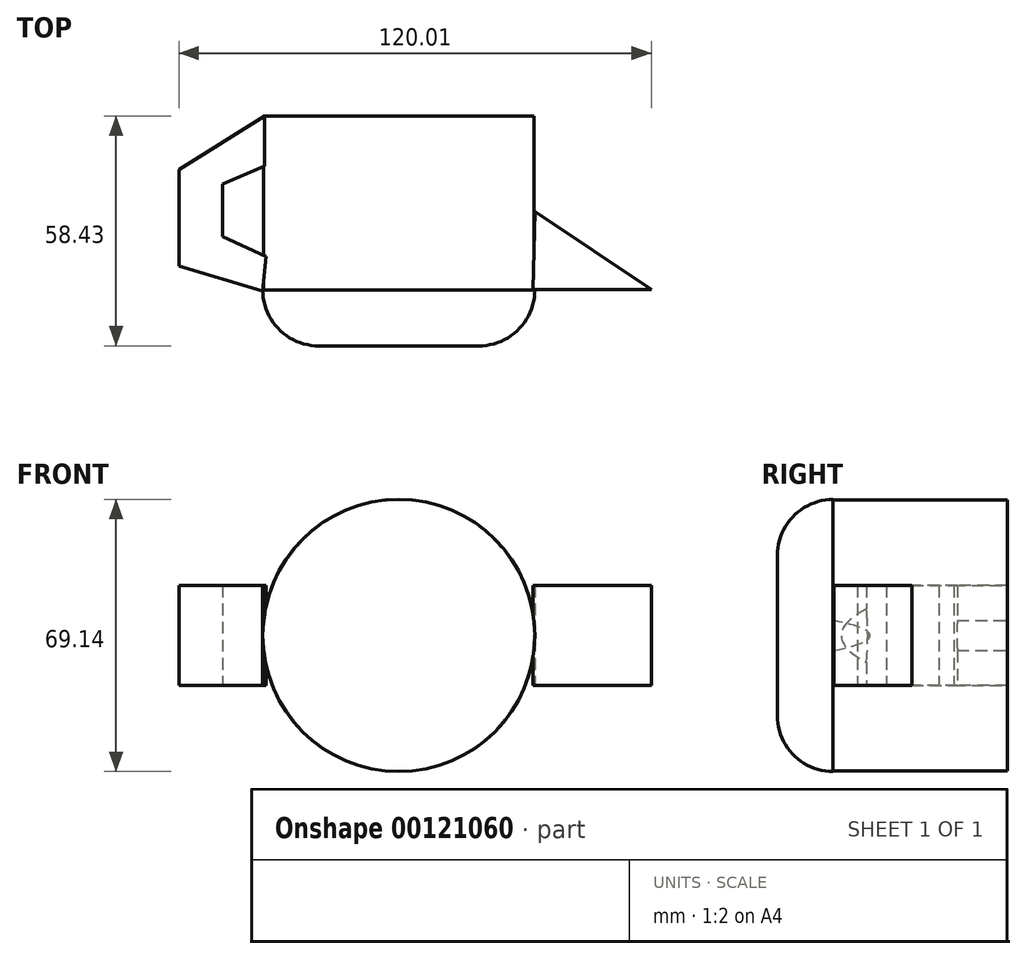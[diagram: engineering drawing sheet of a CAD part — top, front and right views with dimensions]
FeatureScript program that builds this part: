
annotation { "Feature Type Name" : "Feature", "Feature Type Description" : "" }
export const myFeature = defineFeature(function(context is Context, id is Id, definition is map)
    precondition{}
    {
        {
            var Q0;
            Q0=qCreatedBy(makeId("Front.planeOp"),FACE);
            var sketch = newSketch(context, id + "F0", { "sketchPlane" : qUnion([Q0])});
            skCircle(sketch, "E0", {"center": v(0, 0) * mm, "radius": 34.37 * mm});
            skSolve(sketch);
        }
        {
            var Q0;
            Q0 = qSketchRegion(id + "F0", true);
            extrude(context, id + "F1", {"entities" : qUnion([Q0]), "depth" : 44.3 * mm});
        }
        {
            var Q0;
            Q0=makeQuery(id+"F1.opExtrude","CAP_FACE",FACE,{"disambiguationData":[OSD([sQuery(id+"F0.wireOp",EDGE,"E0")])],"isStart":false});
            var sketch = newSketch(context, id + "F2", { "sketchPlane" : qUnion([Q0])});
            skCircle(sketch, "E1", {"center": v(0, 0) * mm, "radius": 34.57 * mm});
            skSolve(sketch);
        }
        {
            var Q0;
            Q0 = qSketchRegion(id + "F2", true);
            extrude(context, id + "F3", {"entities" : qUnion([Q0]), "operationType" : NewBodyOperationType.ADD, "depth" : 14.14 * mm});
        }
        {
            var Q0;
            Q0=makeQuery(id+"F3.opExtrude","CAP_EDGE",EDGE,{"disambiguationData":[OSD([sQuery(id+"F2.wireOp",EDGE,"E1")])],"isStart":false});
            fillet(context, id + "F4", {"entities" : qUnion([Q0]), "radius" : 14.22 * mm, "tangentPropagation" : true, "allowEdgeOverflow" : false});
        }
        {
            var Q0;
            Q0=qCreatedBy(makeId("Top.planeOp"),FACE);
            var sketch = newSketch(context, id + "F5", { "sketchPlane" : qUnion([Q0])});
            skLineSegment(sketch, "E2", {"start": v(34.16, -44.08) * mm, "end": v(64.16, -44.08) * mm});
            skLineSegment(sketch, "E3", {"start": v(64.16, -44.08) * mm, "end": v(34.62, -24.23) * mm});
            skLineSegment(sketch, "E4", {"start": v(34.62, -24.23) * mm, "end": v(34.16, -44.08) * mm});
            skSolve(sketch);
        }
        {
            var Q0;
            Q0=makeQuery(id+"F5.imprint","IMPRINT",FACE,{"disambiguationData":[TD([[makeQuery(id+"F5.imprint","IMPRINT",EDGE,{"derivedFrom":sQuery(id+"F5.wireOp",EDGE,"E2")}),1.0]])]});
            extrude(context, id + "F6", {"entities" : qUnion([Q0]), "operationType" : NewBodyOperationType.ADD, "endBound" : BoundingType.SYMMETRIC, "depth" : 25.4 * mm});
        }
        {
            var Q0;
            Q0=qCreatedBy(makeId("Top.planeOp"),FACE);
            var sketch = newSketch(context, id + "F7", { "sketchPlane" : qUnion([Q0])});
            skLineSegment(sketch, "E5", {"start": v(-34.62, -44.54) * mm, "end": v(-55.85, -38.08) * mm});
            skLineSegment(sketch, "E6", {"start": v(-55.85, -38.08) * mm, "end": v(-55.85, -13.62) * mm});
            skLineSegment(sketch, "E7", {"start": v(-55.85, -13.62) * mm, "end": v(-34.16, 0) * mm});
            skLineSegment(sketch, "E8", {"start": v(-34.16, 0) * mm, "end": v(-34.16, -12.7) * mm});
            skLineSegment(sketch, "E9", {"start": v(-34.16, -12.7) * mm, "end": v(-44.77, -17.3) * mm});
            skLineSegment(sketch, "E10", {"start": v(-44.77, -17.3) * mm, "end": v(-44.77, -30.7) * mm});
            skLineSegment(sketch, "E11", {"start": v(-44.77, -30.7) * mm, "end": v(-33.7, -35.77) * mm});
            skLineSegment(sketch, "E12", {"start": v(-33.7, -35.77) * mm, "end": v(-34.62, -44.54) * mm});
            skSolve(sketch);
        }
        {
            var Q0;
            Q0=makeQuery(id+"F7.imprint","IMPRINT",FACE,{"disambiguationData":[TD([[makeQuery(id+"F7.imprint","IMPRINT",EDGE,{"derivedFrom":sQuery(id+"F7.wireOp",EDGE,"E5")}),-1.0]])]});
            extrude(context, id + "F8", {"entities" : qUnion([Q0]), "operationType" : NewBodyOperationType.ADD, "endBound" : BoundingType.SYMMETRIC, "depth" : 25.4 * mm});
        }
    });
